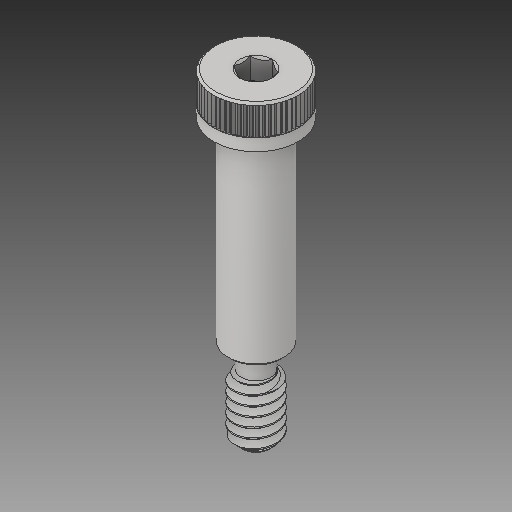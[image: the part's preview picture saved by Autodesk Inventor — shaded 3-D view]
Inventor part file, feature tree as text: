
AUTODESK INVENTOR PART (.ipt)
format: ipt  version: 2017 (Build 210142000, 142)  size: 572,416 bytes
history: mixed  units: in
note: dims shown in document units (in); Inventor stores cm internally (conversion verified against a paired STEP export)
features: chamfer x1, imported_body x1
ambient origin geometry x8: Origin, YZ Plane, XZ Plane, XY Plane, X Axis, Y Axis, Z Axis, Center Point
bodies: Solid1 (imported_parasolid)
feature tree (2):
  chamfer  "Chamfer3"  [1 undecoded]
  imported_body  NMx_Import_Brep_tag  [imported B-rep: ~22 faces, bbox_mm=[7.136728, 26.9875, 7.584722]]
note: 1 required parameter value undecoded (feature->parameter linkage not recoverable at this tier; creation-order binding heuristic only, values carry confidence <= 0.55)
